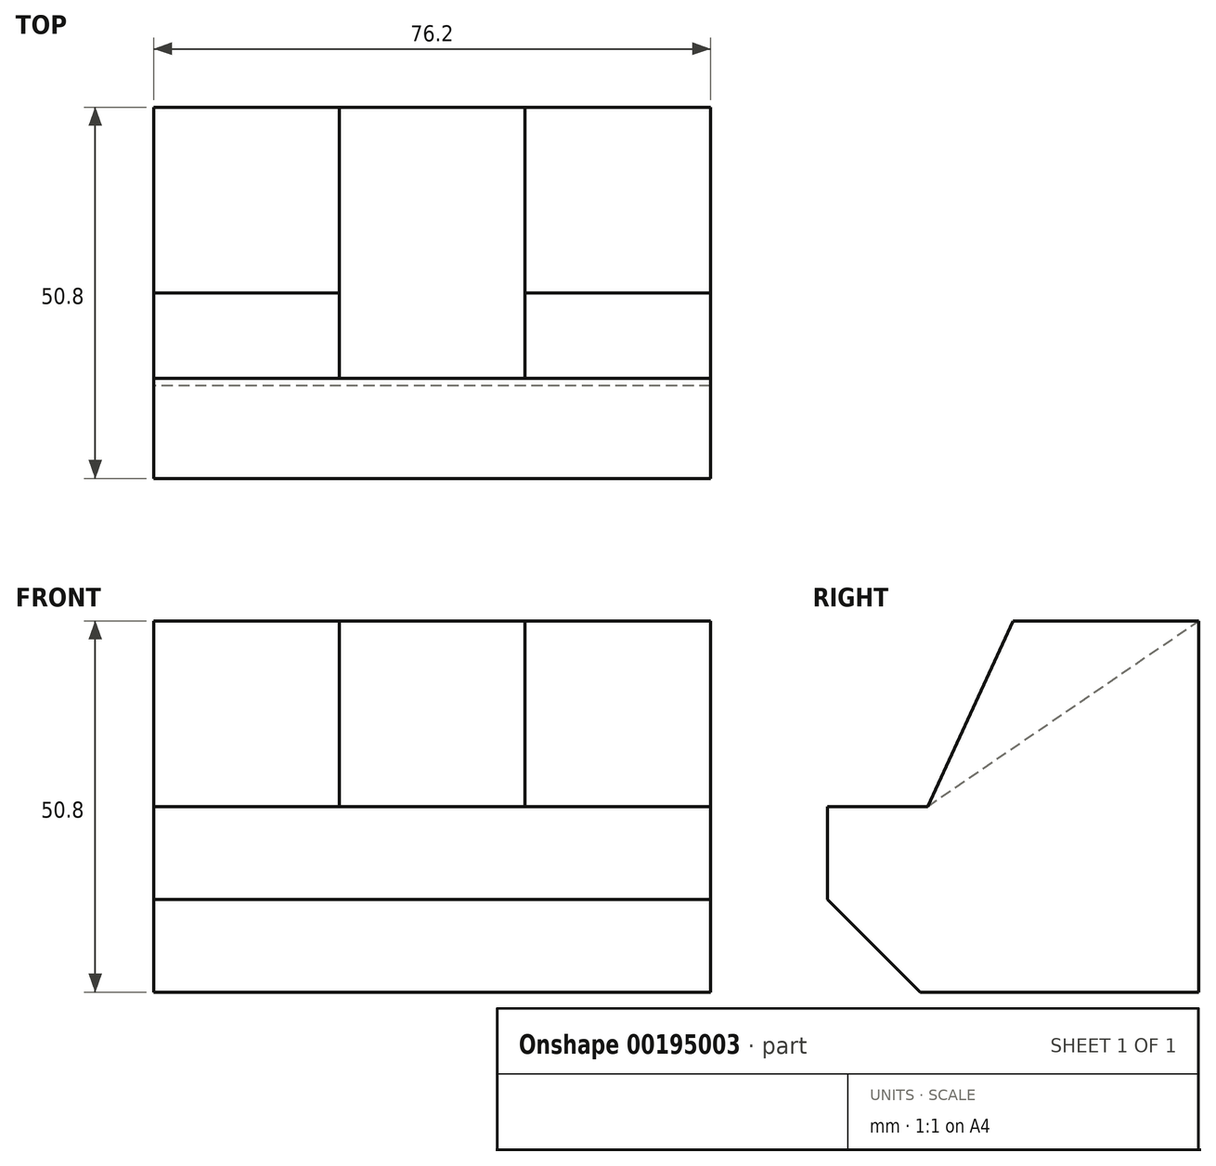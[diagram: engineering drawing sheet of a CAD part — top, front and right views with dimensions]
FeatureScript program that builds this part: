
annotation { "Feature Type Name" : "Feature", "Feature Type Description" : "" }
export const myFeature = defineFeature(function(context is Context, id is Id, definition is map)
    precondition{}
    {
        {
            var Q0;
            Q0=qCreatedBy(makeId("Right.planeOp"),FACE);
            var sketch = newSketch(context, id + "F0", { "sketchPlane" : qUnion([Q0])});
            skLineSegment(sketch, "E0", {"start": v(0, 0) * mm, "end": v(-38.1, 0) * mm});
            skLineSegment(sketch, "E1", {"start": v(-38.1, 0) * mm, "end": v(-50.8, 12.7) * mm});
            skLineSegment(sketch, "E2", {"start": v(-50.8, 12.7) * mm, "end": v(-50.8, 25.4) * mm});
            skLineSegment(sketch, "E3", {"start": v(-50.8, 25.4) * mm, "end": v(-37.12, 25.4) * mm});
            skLineSegment(sketch, "E4", {"start": v(-37.12, 25.4) * mm, "end": v(-25.4, 50.8) * mm});
            skLineSegment(sketch, "E5", {"start": v(-25.4, 50.8) * mm, "end": v(0, 50.8) * mm});
            skLineSegment(sketch, "E6", {"start": v(0, 50.8) * mm, "end": v(0, 0) * mm});
            skSolve(sketch);
        }
        {
            var Q0;
            Q0 = qSketchRegion(id + "F0", true);
            extrude(context, id + "F1", {"entities" : qUnion([Q0]), "depth" : 76.2 * mm});
        }
        {
            var Q0;
            Q0=makeQuery(id+"F1.opExtrude","CAP_FACE",FACE,{"disambiguationData":[OSD([sQuery(id+"F0.wireOp",EDGE,"E0"),sQuery(id+"F0.wireOp",EDGE,"E1"),sQuery(id+"F0.wireOp",EDGE,"E2"),sQuery(id+"F0.wireOp",EDGE,"E3"),sQuery(id+"F0.wireOp",EDGE,"E4"),sQuery(id+"F0.wireOp",EDGE,"E5"),sQuery(id+"F0.wireOp",EDGE,"E6")])],"isStart":false});
            var Q1;
            Q1=makeQuery(id+"F1.opExtrude","CAP_FACE",FACE,{"disambiguationData":[OSD([sQuery(id+"F0.wireOp",EDGE,"E0"),sQuery(id+"F0.wireOp",EDGE,"E1"),sQuery(id+"F0.wireOp",EDGE,"E2"),sQuery(id+"F0.wireOp",EDGE,"E3"),sQuery(id+"F0.wireOp",EDGE,"E4"),sQuery(id+"F0.wireOp",EDGE,"E5"),sQuery(id+"F0.wireOp",EDGE,"E6")])],"isStart":true});
            cPlane(context, id + "F2", {"entities" : qUnion([Q0, Q1]), "cplaneType" : CPlaneType.MID_PLANE, "offset" : 25.4 * mm, "width" : 152.4 * mm, "height" : 152.4 * mm});
        }
        {
            var Q0;
            Q0=qCreatedBy(id+"F2.planeOp",FACE);
            var sketch = newSketch(context, id + "F3", { "sketchPlane" : qUnion([Q0])});
            skLineSegment(sketch, "E7", {"start": v(-37.12, 25.4) * mm, "end": v(0, 50.8) * mm});
            skLineSegment(sketch, "E8", {"start": v(0, 50.8) * mm, "end": v(-25.4, 50.8) * mm});
            skLineSegment(sketch, "E9", {"start": v(-25.4, 50.8) * mm, "end": v(-37.12, 25.4) * mm});
            skSolve(sketch);
        }
        {
            var Q0;
            Q0 = qSketchRegion(id + "F3", true);
            extrude(context, id + "F4", {"entities" : qUnion([Q0]), "operationType" : NewBodyOperationType.REMOVE, "oppositeDirection" : true, "depth" : 12.7 * mm, "hasSecondDirection" : true, "secondDirectionOppositeDirection" : false, "secondDirectionDepth" : 12.7 * mm});
        }
    });
